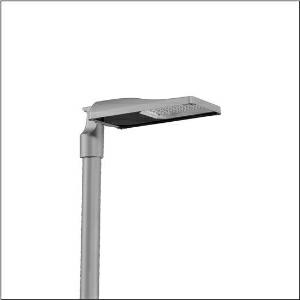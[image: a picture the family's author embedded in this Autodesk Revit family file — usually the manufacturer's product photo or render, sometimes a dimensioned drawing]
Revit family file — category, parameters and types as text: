
# Revit family: streetlight_sl_31_mini___st1_0a_5xh2d3ab08ja_f81c
name_source: partatom
category: Lighting Fixtures
units: mm (PartAtom-declared; Revit-internal decimal feet)

## family parameters
Cut with Voids When Loaded = No
Host = Face
Light Source = No
Part Type = Normal
Room Calculation Point = No
Round Connector Dimension = Use Diameter
Shared = No

## types (1)
- --- (1 x LED, 12140 lm, 81.1 W, 3000K)
    Apparent Load = 81 VA
    CIE Flux Codes = 40 73 97 100 100
    Color Rendering = 70
    Color Temperature = 3000K
    Default Elevation = 1800 mm
    Description = Streetlight SL 31 mini Easy LST mast luminaire for post-top, side-entry; light control with lens of PMMA; light distribution: ST1.0a, direct asymmetric distribution, for standard-compliant lighting for roads and squares; LED: luminous flux: 12.140lm, light colour: 730, colour temperature: 3000K; luminous efficacy: 149,7lm/W; control: pre-setting: linear dimming characteristic, flexible luminous flux parameterisation, time-dependent luminous flux control, constant luminous flux control, power reduction, intelligent temperature release in ECG and LED module, overheat protection; luminaire housing, of diecast aluminium, SITECO metallic grey (DB 702S), corrosivity category C5 high according to DIN EN ISO 12944; cover of toughened safety glass, transparent, mast flange of diecast aluminium, SITECO metallic grey (DB 702S), spigot size: 76/60mm, mast flange included unmounted; cable length: 10,5m, connection cable pre-assembled; mains connection: 220..240V, AC, 50/60Hz; power consumption (at start of service life): 81,1W / (at end of service life): 88,3W / (with reduced operation 50%): 36,4W; protection rating (complete): IP66; insulation class (complete): insulation class II (safety insulation); impact resistance: IK10; certification: CE, ENEC, ENEC+, VDE, UKCA; permissible operating ambient temperature for outdoor applications: -40..+50°C; packaging unit: 1 piece

Light Distribution: ST1.0a
    Height = 76 mm
    Lamp = 1 x LED
    Lamp Light Flux = 12140 lm
    Lamp Power = 81.1 W
    Lamp count = 1
    Length = 547 mm
    Luminous efficacy = 150 lm/W
    Manufacturer = Siteco
    ModVariant = No
    Model = 5XH2D3AB08JA
    Number of Poles = 1
    OnlyDefault = Yes
    Power Factor = 1
    Product Name = Streetlight SL 31 mini | ST1.0a
    Product group = mast luminaire | pylon top
    ProductGroupID = 6100
    Protection Class = Protection class II
    Protection Degree = IP 66
    RLX_Detail_Level = 1
    RLX_Emergency_Light_Flux = 0 lm
    RLX_Emergency_Type = 0
    RLX_Emergency_Type_DB = No
    RlxData = <blob elided: 39617 chars, md5=e71c7ca9>
    Socket = socket
    Standby Power = 0 W
    System Light Flux = 12140 lm
    System Power = 81 W
    Type Comments = factory setting: luminous flux: 100 % | dim-lin: 254 | 860 mA
    Type Image = l_1300326.jpg
    URL = http://relux.com
    VarID = @adj_057835
    Voltage = 0 V
    Weight = 0.00 kg
    Width = 265 mm

## geometry (parser evidence)
native form markers: Blend x4, Sweep x11
no freeform markers — native parametric forms only
